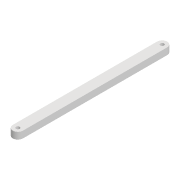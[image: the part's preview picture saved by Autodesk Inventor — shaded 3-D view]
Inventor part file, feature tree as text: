
AUTODESK INVENTOR PART (.ipt)
format: ipt  version: 2022 (Build 260153000, 153)  size: 89,088 bytes
history: native  units: mm
features: extrude x1, sketch x1
ambient origin geometry x8: Origin, YZ Plane, XZ Plane, XY Plane, X Axis, Y Axis, Z Axis, Center Point
bodies: Solid1 (feature_tree)
feature tree (2):
  extrude  "Extrusion1"  Depth=4.0mm
  sketch  "Sketch1"  dims[d0=2.2mm d1=2.2mm d2=6.0mm d3=85.9mm d6=4.0mm d7=0.0mm]
